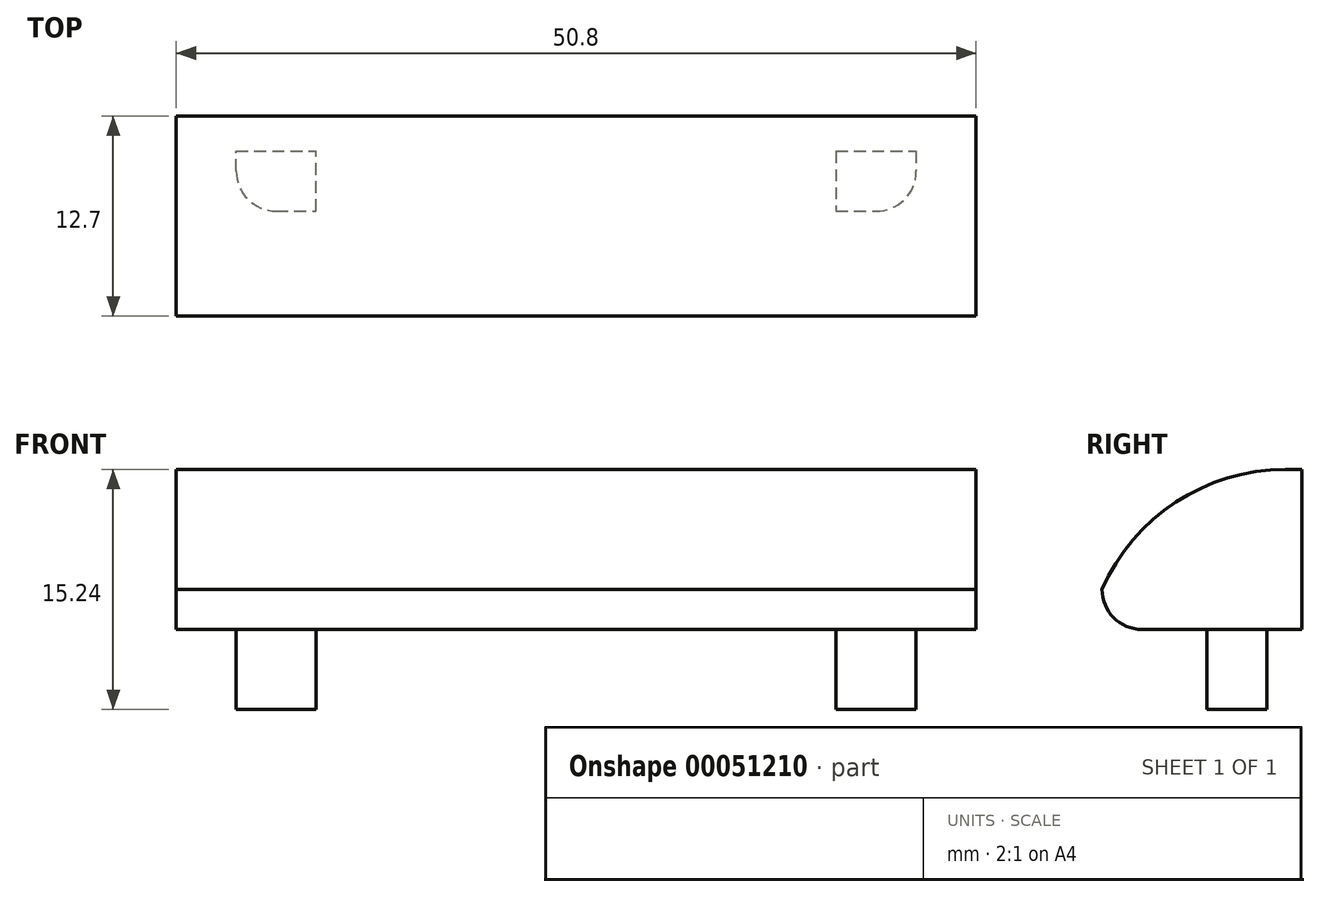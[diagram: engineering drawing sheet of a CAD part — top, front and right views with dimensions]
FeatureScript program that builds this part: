
annotation { "Feature Type Name" : "Feature", "Feature Type Description" : "" }
export const myFeature = defineFeature(function(context is Context, id is Id, definition is map)
    precondition{}
    {
        {
            var Q0;
            Q0=qCreatedBy(makeId("Top.planeOp"),FACE);
            var sketch = newSketch(context, id + "F0", { "sketchPlane" : qUnion([Q0])});
            skLineSegment(sketch, "E0.bottom", {"start": v(0, 0) * mm, "end": v(50.8, 0) * mm});
            skLineSegment(sketch, "E0.top", {"start": v(0, 12.7) * mm, "end": v(50.8, 12.7) * mm});
            skLineSegment(sketch, "E0.left", {"start": v(0, 0) * mm, "end": v(0, 12.7) * mm});
            skLineSegment(sketch, "E0.right", {"start": v(50.8, 0) * mm, "end": v(50.8, 12.7) * mm});
            skSolve(sketch);
        }
        {
            var Q0;
            Q0 = qSketchRegion(id + "F0", true);
            extrude(context, id + "F1", {"entities" : qUnion([Q0]), "depth" : 10.16 * mm});
        }
        {
            var Q0;
            Q0=makeQuery(id+"F1.opExtrude","CAP_FACE",FACE,{"disambiguationData":[OSD([sQuery(id+"F0.wireOp",EDGE,"E0.bottom"),sQuery(id+"F0.wireOp",EDGE,"E0.top"),sQuery(id+"F0.wireOp",EDGE,"E0.left"),sQuery(id+"F0.wireOp",EDGE,"E0.right")])],"isStart":true});
            var sketch = newSketch(context, id + "F2", { "sketchPlane" : qUnion([Q0])});
            skLineSegment(sketch, "E1.bottom", {"start": v(3.81, -6.67) * mm, "end": v(8.9, -6.67) * mm});
            skLineSegment(sketch, "E1.top", {"start": v(3.81, -10.48) * mm, "end": v(8.9, -10.48) * mm});
            skLineSegment(sketch, "E1.left", {"start": v(3.81, -6.67) * mm, "end": v(3.81, -10.48) * mm});
            skLineSegment(sketch, "E1.right", {"start": v(8.9, -6.67) * mm, "end": v(8.9, -10.48) * mm});
            skSolve(sketch);
        }
        {
            var Q0;
            Q0 = qSketchRegion(id + "F2", true);
            extrude(context, id + "F3", {"entities" : qUnion([Q0]), "operationType" : NewBodyOperationType.ADD, "depth" : 5.08 * mm});
        }
        {
            var Q0;
            Q0=makeQuery(id+"F1.opExtrude","CAP_FACE",FACE,{"disambiguationData":[OSD([sQuery(id+"F0.wireOp",EDGE,"E0.bottom"),sQuery(id+"F0.wireOp",EDGE,"E0.top"),sQuery(id+"F0.wireOp",EDGE,"E0.left"),sQuery(id+"F0.wireOp",EDGE,"E0.right")])],"isStart":true});
            var sketch = newSketch(context, id + "F4", { "sketchPlane" : qUnion([Q0])});
            skLineSegment(sketch, "E2.bottom", {"start": v(41.91, -10.46) * mm, "end": v(47, -10.46) * mm});
            skLineSegment(sketch, "E2.top", {"start": v(41.91, -6.65) * mm, "end": v(47, -6.65) * mm});
            skLineSegment(sketch, "E2.left", {"start": v(41.91, -10.46) * mm, "end": v(41.91, -6.65) * mm});
            skLineSegment(sketch, "E2.right", {"start": v(47, -10.46) * mm, "end": v(47, -6.65) * mm});
            skSolve(sketch);
        }
        {
            var Q0;
            Q0 = qSketchRegion(id + "F4", true);
            extrude(context, id + "F5", {"entities" : qUnion([Q0]), "operationType" : NewBodyOperationType.ADD, "depth" : 5.08 * mm});
        }
        {
            var Q0;
            Q0=makeQuery(id+"F3.opExtrude","SWEPT_EDGE",EDGE,{"disambiguationData":[OSD([sQuery(id+"F2.wireOp",EDGE,"E1.bottom"),sQuery(id+"F2.wireOp",EDGE,"E1.left")])]});
            var Q1;
            Q1=makeQuery(id+"F5.opExtrude","SWEPT_EDGE",EDGE,{"disambiguationData":[OSD([sQuery(id+"F4.wireOp",EDGE,"E2.top"),sQuery(id+"F4.wireOp",EDGE,"E2.right")])]});
            var Q2;
            Q2=makeQuery(id+"F1.opExtrude","CAP_EDGE",EDGE,{"disambiguationData":[OSD([sQuery(id+"F0.wireOp",EDGE,"E0.bottom")])],"isStart":true});
            fillet(context, id + "F6", {"entities" : qUnion([Q0, Q1, Q2]), "radius" : 2.54 * mm, "tangentPropagation" : true, "allowEdgeOverflow" : false});
        }
        {
            var Q0;
            Q0=makeQuery(id+"F1.opExtrude","CAP_EDGE",EDGE,{"disambiguationData":[OSD([sQuery(id+"F0.wireOp",EDGE,"E0.bottom")])],"isStart":false});
            fillet(context, id + "F7", {"entities" : qUnion([Q0]), "radius" : 12.7 * mm, "tangentPropagation" : true, "allowEdgeOverflow" : false});
        }
    });
